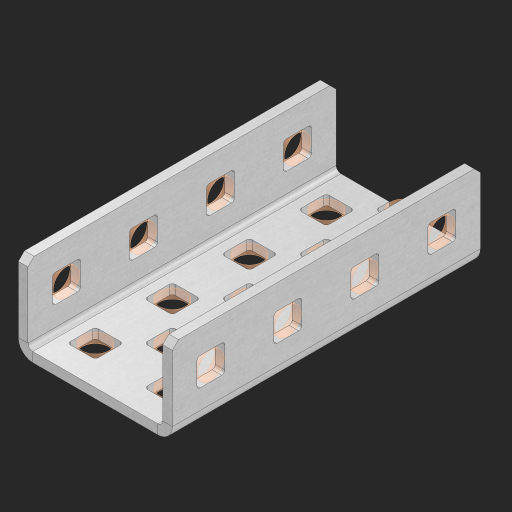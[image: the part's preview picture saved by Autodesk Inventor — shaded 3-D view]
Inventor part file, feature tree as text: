
AUTODESK INVENTOR PART (.ipt)
format: ipt  version: 2023 (Build 270158000, 158)  size: 656,896 bytes
history: native  units: in
note: dims shown in document units (in); Inventor stores cm internally (conversion verified against a paired STEP export)
features: other x27, extrude x18, sheet_metal_op x11, sketch x10, pattern_linear x2, mirror x1, chamfer x1
ambient origin geometry x8: Origin, YZ Plane, XZ Plane, XY Plane, X Axis, Y Axis, Z Axis, Center Point
bodies: Solid1 (feature_tree), Body (feature_tree)
feature tree (70):
  sheet_metal_op  "Flanges"
  other  "Flange Pattern Plane"
  other  "Flange Pattern Sketch"
  sheet_metal_op  "Flange Pattern"
  sheet_metal_op  "Body Pattern"
  pattern_linear  "Center Pattern"  Spacing1=0.0625in  [1 undecoded]
  other  "Arc Length"
  mirror  "Notch Mirror"
  pattern_linear  "Notch Pattern"  Spacing1=0.182in  [1 undecoded]
  chamfer  "End Chamfer"
  extrude  "Half Cut"  Depth=0.02in
  sketch  "Sketch1"  dims[d0=1.0in]
  other  "Plate1"
  sketch  "Sketch2"  dims[d1=2.0in]
  other  "Plate2"
  sheet_metal_op  "Bend1"
  sheet_metal_op  "Corner1"
  sketch  "Sketch3"  dims[d2=0.0625in]
  sketch  "Sketch7"  dims[d3=0.0625in]
  other  "Srf1"
  other  "Srf2"
  sketch  "Sketch8"  dims[d4=0.0312in]
  sketch  "Sketch9"  dims[d5=0.125in]
  other  "Srf91"
  sheet_metal_op  "Body Pattern Sketch"
  other  "Srf92"
  sketch  "Sketch13"  dims[d6=0.0625in]
  sketch  "Sketch14"  dims[d7=0.5in d8=90.0deg d9=0.0312in]
  sketch  "Sketch15"  dims[d10=0.25in]
  sketch  "Sketch16"  dims[d11=0.0625in d12=0.0625in d16=0.182in d17=0.02in d18=0.0625in d19=0.0in d20=0.25in d21=0.25in d38=1.5748in d40=0.5in d41=0.7874in d43=1.0in d46=0.172in d47=1.0in d48=0.0in d49=0.182in d50=0.02in d51=0.25in d52=0.25in d53=0.0625in d54=0.0in d55=0.172in d56=1.0in d57=0.0in d58=0.25in d60=1.5748in d62=0.5in d63=0.7874in d65=0.5in d85=0.1473in d86=0.1782in d88=0.04in d89=0.0625in d90=0.0in d91=0.04in d92=0.0491in d95=2.5in d96=0.04in d97=0.25in d98=45.0deg d99=0.25in d100=0.5in d101=0.0in d102=2.497in d106=0.182in d107=0.02in d108=0.5in d109=0.5in d110=0.0625in d111=0.0in d112=0.172in d113=0.5in d114=0.0in d117=0.5in d118=0.5in d119=0.5in]
  other  "Srf786"
  other  "Srf823"
  other  "Srf824"
  other  "Srf825"
  other  "Srf826"
  other  "Srf827"
  other  "Srf828"
  other  "Srf856"
  other  "Srf857"
  other  "Srf858"
  other  "Srf859"
  other  "Srf860"
  other  "Srf861"
  other  "Srf889"
  other  "Srf890"
  other  "Srf891"
  sheet_metal_op  "Flange Stamp"
  sheet_metal_op  "Flange Circle"
  sheet_metal_op  "Body Stamp"
  sheet_metal_op  "Body Circle"
  other  "Center Stamp"
  other  "Center Circle"
  sheet_metal_op  "Notch"
  extrude  "ExtrusionSrf2"  Depth=0.0625in
  extrude  "ExtrusionSrf92"  TaperAngle=0.0deg  [1 undecoded]
  extrude  "ExtrusionSrf823"  Depth=0.25in
  extrude  "ExtrusionSrf824"  Depth=0.25in
  extrude  "ExtrusionSrf825"  Depth=0.5in
  extrude  "ExtrusionSrf826"  Depth=0.5in
  extrude  "ExtrusionSrf827"  Depth=1.0in TaperAngle=0.0deg
  extrude  "ExtrusionSrf828"  Depth=0.182in
  extrude  "ExtrusionSrf856"  Depth=0.02in
  extrude  "ExtrusionSrf857"  Depth=0.25in
  extrude  "ExtrusionSrf858"  Depth=0.25in
  extrude  "ExtrusionSrf859"  Depth=0.0625in
  extrude  "ExtrusionSrf860"  TaperAngle=0.0deg  [1 undecoded]
  extrude  "ExtrusionSrf861"  Depth=0.5in
  extrude  "ExtrusionSrf889"  Depth=1.0in TaperAngle=0.0deg
  extrude  "ExtrusionSrf890"  Depth=0.25in
  extrude  "ExtrusionSrf891"  Depth=0.5in
note: 4 required parameter values undecoded (feature->parameter linkage not recoverable at this tier; creation-order binding heuristic only, values carry confidence <= 0.55)
